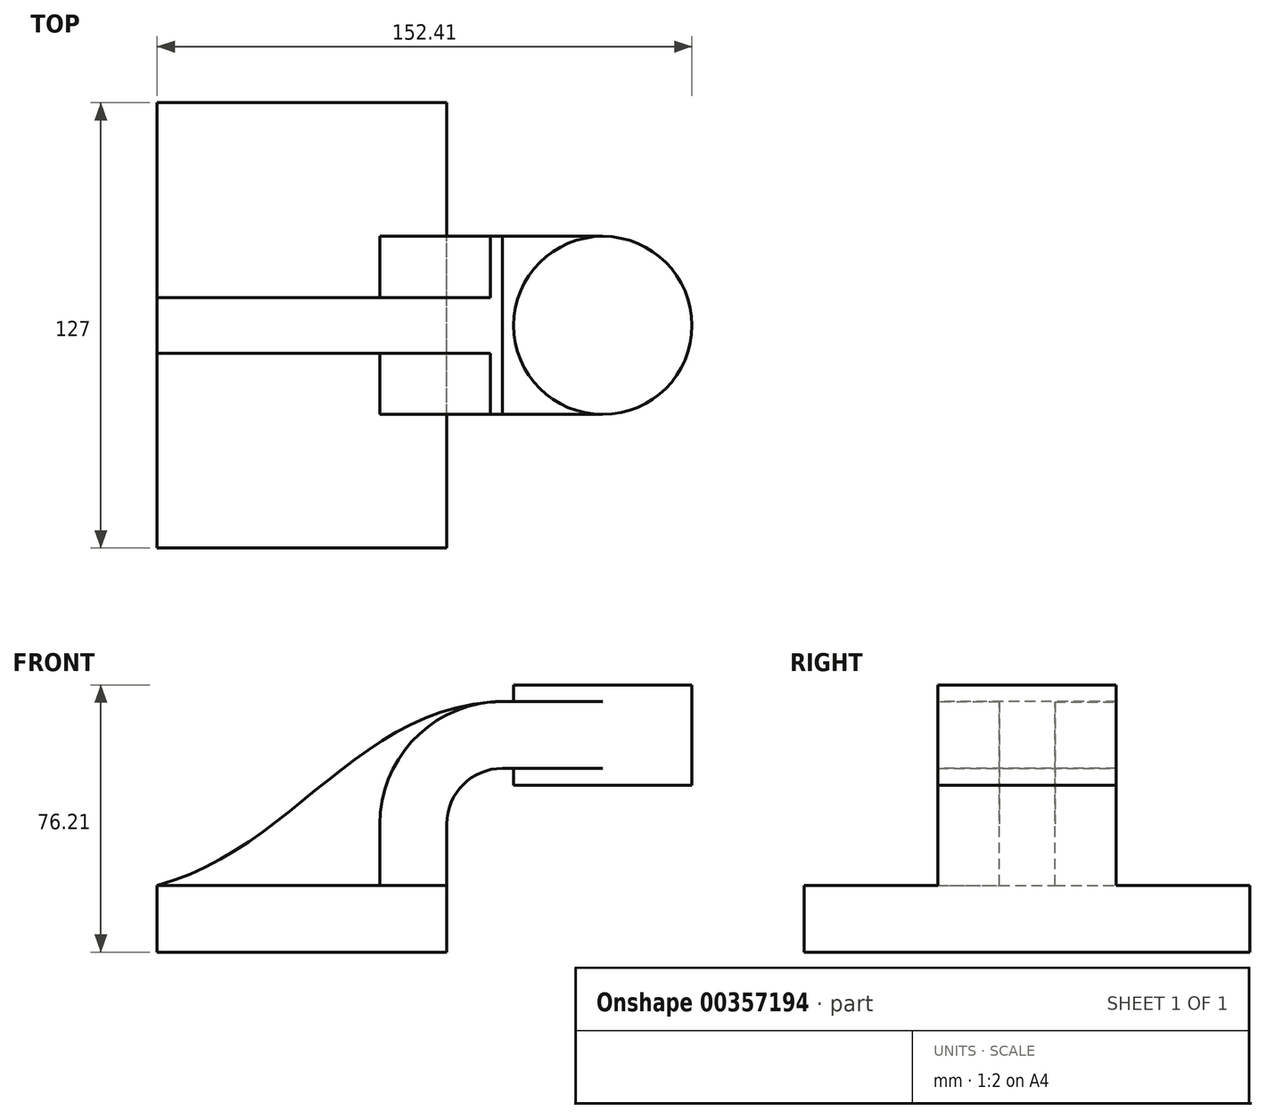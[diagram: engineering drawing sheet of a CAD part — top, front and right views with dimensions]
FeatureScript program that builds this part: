
annotation { "Feature Type Name" : "Feature", "Feature Type Description" : "" }
export const myFeature = defineFeature(function(context is Context, id is Id, definition is map)
    precondition{}
    {
        {
            var Q0;
            Q0=qCreatedBy(makeId("Front.planeOp"),FACE);
            var sketch = newSketch(context, id + "F0", { "sketchPlane" : qUnion([Q0])});
            skLineSegment(sketch, "E0.bottom", {"start": v(-41.28, -9.53) * mm, "end": v(41.28, -9.53) * mm});
            skLineSegment(sketch, "E0.top", {"start": v(-41.28, 9.52) * mm, "end": v(41.28, 9.52) * mm});
            skLineSegment(sketch, "E0.left", {"start": v(-41.28, -9.53) * mm, "end": v(-41.28, 9.52) * mm});
            skLineSegment(sketch, "E0.right", {"start": v(41.28, -9.53) * mm, "end": v(41.28, 9.52) * mm});
            skPoint(sketch, "E0.middle", {"position": v(0, 0) * mm});
            skLineSegment(sketch, "E1.bottom", {"start": v(111.12, 38.1) * mm, "end": v(60.32, 38.1) * mm});
            skLineSegment(sketch, "E1.top", {"start": v(111.12, 66.68) * mm, "end": v(60.32, 66.68) * mm});
            skLineSegment(sketch, "E1.left", {"start": v(111.12, 38.1) * mm, "end": v(111.12, 66.68) * mm});
            skLineSegment(sketch, "E1.right", {"start": v(60.32, 38.1) * mm, "end": v(60.32, 66.68) * mm});
            skPoint(sketch, "E1.middle", {"position": v(85.72, 52.39) * mm});
            skLineSegment(sketch, "E2", {"start": v(41.28, 9.52) * mm, "end": v(41.28, 27) * mm});
            skArc(sketch, "E3", {"start": v(41.27, 27) * mm, "mid": v(45.92, 38.23) * mm, "end": v(57.15, 42.88) * mm});
            skLineSegment(sketch, "E4", {"start": v(57.15, 42.88) * mm, "end": v(85.72, 42.88) * mm});
            skLineSegment(sketch, "E5.0", {"start": v(57.15, 61.93) * mm, "end": v(85.72, 61.93) * mm});
            skArc(sketch, "E5.1", {"start": v(22.23, 27) * mm, "mid": v(32.45, 51.7) * mm, "end": v(57.15, 61.93) * mm});
            skLineSegment(sketch, "E5.2", {"start": v(22.23, 9.52) * mm, "end": v(22.23, 27) * mm});
            skLineSegment(sketch, "E6", {"start": v(85.72, 61.93) * mm, "end": v(85.72, 42.88) * mm});
            skLineSegment(sketch, "E7", {"start": v(41.28, 9.52) * mm, "end": v(22.23, 9.52) * mm});
            skFitSpline(sketch, "E8", {"points": [v(-41.28, 9.53) * mm, v(57.15, 61.93) * mm], "startDerivative": vector(114.96, 29.63) * mm, "endDerivative": vector(122.93, 2.56) * mm});
            skLineSegment(sketch, "E9", {"start": v(85.72, 61.93) * mm, "end": v(85.72, 66.68) * mm});
            skLineSegment(sketch, "E10", {"start": v(85.72, 42.88) * mm, "end": v(85.72, 38.1) * mm});
            skSolve(sketch);
        }
        {
            var Q0;
            Q0=makeQuery(id+"F0.imprint","IMPRINT",FACE,{"disambiguationData":[TD([[makeQuery(id+"F0.imprint","IMPRINT",EDGE,{"derivedFrom":sQuery(id+"F0.wireOp",EDGE,"E0.bottom")}),1.0]])]});
            extrude(context, id + "F1", {"entities" : qUnion([Q0]), "endBound" : BoundingType.SYMMETRIC, "depth" : 127 * mm});
        }
        {
            var Q0;
            {var subQ0=sQuery(id+"F0.wireOp",EDGE,"E0.top");Q0=makeQuery(id+"F0.imprint","IMPRINT",FACE,{"disambiguationData":[TD([[makeQuery(id+"F0.imprint","IMPRINT",EDGE,{"derivedFrom":subQ0}),1.0]])]});}
            extrude(context, id + "F2", {"entities" : qUnion([Q0]), "operationType" : NewBodyOperationType.ADD, "endBound" : BoundingType.SYMMETRIC, "depth" : 15.88 * mm});
        }
        {
            var Q0;
            Q0=makeQuery(id+"F0.imprint","IMPRINT",FACE,{"disambiguationData":[TD([[makeQuery(id+"F0.imprint","IMPRINT",EDGE,{"derivedFrom":sQuery(id+"F0.wireOp",EDGE,"E2")}),1.0]])]});
            var Q1;
            {var subQ5=sQuery(id+"F0.wireOp",EDGE,"E6");Q1=makeQuery(id+"F0.imprint","IMPRINT",FACE,{"disambiguationData":[TD([[makeQuery(id+"F0.imprint","IMPRINT",EDGE,{"derivedFrom":subQ5}),-1.0]])]});}
            extrude(context, id + "F3", {"entities" : qUnion([Q0, Q1]), "operationType" : NewBodyOperationType.ADD, "endBound" : BoundingType.SYMMETRIC, "depth" : 50.8 * mm});
        }
        {
            var Q0;
            {var subQ0=sQuery(id+"F0.wireOp",EDGE,"E1.left");Q0=makeQuery(id+"F0.imprint","IMPRINT",FACE,{"disambiguationData":[TD([[makeQuery(id+"F0.imprint","IMPRINT",EDGE,{"derivedFrom":subQ0}),1.0]])]});}
            var Q1;
            Q1=sQuery(id+"F0.wireOp",EDGE,"E6");
            revolve(context, id + "F4", {"operationType" : NewBodyOperationType.ADD, "entities" : qUnion([Q0]), "axis" : qUnion([Q1]), "revolveType" : RevolveType.FULL});
        }
    });
